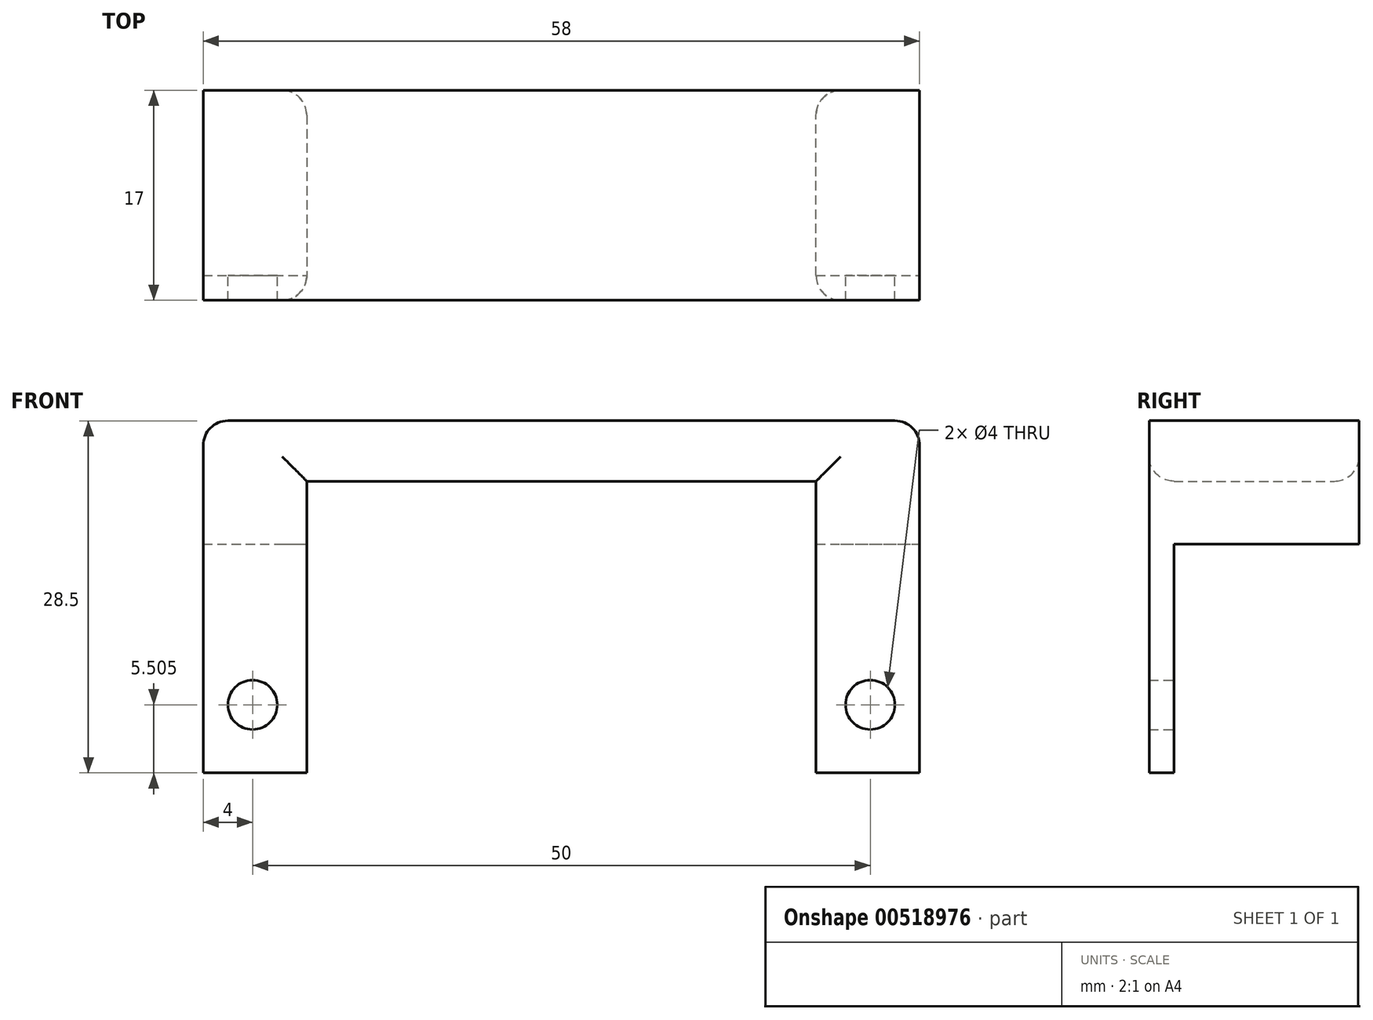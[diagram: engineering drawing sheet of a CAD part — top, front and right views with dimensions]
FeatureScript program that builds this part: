
annotation { "Feature Type Name" : "Feature", "Feature Type Description" : "" }
export const myFeature = defineFeature(function(context is Context, id is Id, definition is map)
    precondition{}
    {
        {
            var Q0;
            Q0=qCreatedBy(makeId("Front.planeOp"),FACE);
            var sketch = newSketch(context, id + "F0", { "sketchPlane" : qUnion([Q0])});
            skLineSegment(sketch, "E0.bottom", {"start": v(-17.8, 17.5) * mm, "end": v(40.2, 17.5) * mm});
            skLineSegment(sketch, "E0.left", {"start": v(-17.8, 17.5) * mm, "end": v(-17.8, -11) * mm});
            skLineSegment(sketch, "E0.right", {"start": v(40.2, 17.5) * mm, "end": v(40.2, -11) * mm});
            skLineSegment(sketch, "E1", {"start": v(-17.8, 7.5) * mm, "end": v(40.2, 7.5) * mm, "construction": true});
            skCircle(sketch, "E2", {"center": v(-13.8, -5.5) * mm, "radius": 2 * mm});
            skCircle(sketch, "E3", {"center": v(36.2, -5.5) * mm, "radius": 2 * mm});
            skLineSegment(sketch, "E4.top", {"start": v(-9.42, 12.6) * mm, "end": v(31.8, 12.6) * mm});
            skLineSegment(sketch, "E4.left", {"start": v(-9.42, -11) * mm, "end": v(-9.42, 12.6) * mm});
            skLineSegment(sketch, "E4.right", {"start": v(31.8, -11) * mm, "end": v(31.8, 12.6) * mm});
            skLineSegment(sketch, "E5", {"start": v(-9.42, -11) * mm, "end": v(-17.8, -11) * mm});
            skLineSegment(sketch, "E6", {"start": v(31.8, -11) * mm, "end": v(40.2, -11) * mm});
            skSolve(sketch);
        }
        {
            var Q0;
            Q0=makeQuery(id+"F0.imprint","IMPRINT",FACE,{"disambiguationData":[TD([[makeQuery(id+"F0.imprint","IMPRINT",EDGE,{"derivedFrom":sQuery(id+"F0.wireOp",EDGE,"E0.bottom")}),-1.0]])]});
            extrude(context, id + "F1", {"entities" : qUnion([Q0]), "depth" : 2 * mm, "offsetDistance" : 25 * mm});
        }
        {
            var Q0;
            Q0=makeQuery(id+"F0.imprint","IMPRINT",FACE,{"disambiguationData":[TD([[makeQuery(id+"F0.imprint","IMPRINT",EDGE,{"derivedFrom":sQuery(id+"F0.wireOp",EDGE,"E0.bottom")}),-1.0]])]});
            var sketch = newSketch(context, id + "F2", { "sketchPlane" : qUnion([Q0])});
            skLineSegment(sketch, "E7", {"start": v(40.2, 7.5) * mm, "end": v(40.2, 17.5) * mm});
            skLineSegment(sketch, "E8", {"start": v(40.2, 17.5) * mm, "end": v(-17.8, 17.5) * mm});
            skLineSegment(sketch, "E9", {"start": v(-17.8, 17.5) * mm, "end": v(-17.8, 7.5) * mm});
            skLineSegment(sketch, "E10", {"start": v(-17.8, 7.5) * mm, "end": v(-9.42, 7.5) * mm});
            skLineSegment(sketch, "E11", {"start": v(-9.42, 7.5) * mm, "end": v(-9.42, 12.6) * mm});
            skLineSegment(sketch, "E12", {"start": v(-9.42, 12.6) * mm, "end": v(31.8, 12.6) * mm});
            skLineSegment(sketch, "E13", {"start": v(31.8, 12.6) * mm, "end": v(31.8, 7.5) * mm});
            skLineSegment(sketch, "E14", {"start": v(31.8, 7.5) * mm, "end": v(40.2, 7.5) * mm});
            skSolve(sketch);
        }
        {
            var Q0;
            Q0=makeQuery(id+"F2.imprint","IMPRINT",FACE,{"disambiguationData":[TD([[makeQuery(id+"F2.imprint","IMPRINT",EDGE,{"derivedFrom":sQuery(id+"F2.wireOp",EDGE,"E7")}),-1.0]])]});
            extrude(context, id + "F3", {"entities" : qUnion([Q0]), "operationType" : NewBodyOperationType.ADD, "oppositeDirection" : true, "depth" : 15 * mm, "offsetDistance" : 25 * mm});
        }
        {
            var Q0;
            Q0=makeQuery(id+"F3.boolean.opBoolean","MERGE",EDGE,{"derivedFrom":[makeQuery(id+"F1.opExtrude","SWEPT_EDGE",EDGE,{"disambiguationData":[OSD([sQuery(id+"F0.wireOp",EDGE,"E0.bottom"),sQuery(id+"F0.wireOp",EDGE,"E0.left")])]}),makeQuery(id+"F3.opExtrude","SWEPT_EDGE",EDGE,{"disambiguationData":[OSD([sQuery(id+"F2.wireOp",EDGE,"E8"),sQuery(id+"F2.wireOp",EDGE,"E9")])]})]});
            var Q1;
            Q1=makeQuery(id+"F3.boolean.opBoolean","MERGE",EDGE,{"derivedFrom":[makeQuery(id+"F1.opExtrude","SWEPT_EDGE",EDGE,{"disambiguationData":[OSD([sQuery(id+"F0.wireOp",EDGE,"E0.bottom"),sQuery(id+"F0.wireOp",EDGE,"E0.right")])]}),makeQuery(id+"F3.opExtrude","SWEPT_EDGE",EDGE,{"disambiguationData":[OSD([sQuery(id+"F2.wireOp",EDGE,"E7"),sQuery(id+"F2.wireOp",EDGE,"E8")])]})]});
            var Q2;
            Q2=makeQuery(id+"F1.opExtrude","CAP_EDGE",EDGE,{"disambiguationData":[OSD([sQuery(id+"F0.wireOp",EDGE,"E4.top")])],"isStart":false});
            var Q3;
            Q3=makeQuery(id+"F1.opExtrude","CAP_EDGE",EDGE,{"disambiguationData":[OSD([sQuery(id+"F0.wireOp",EDGE,"E4.right")])],"isStart":false});
            var Q4;
            Q4=makeQuery(id+"F1.opExtrude","CAP_EDGE",EDGE,{"disambiguationData":[OSD([sQuery(id+"F0.wireOp",EDGE,"E4.left")])],"isStart":false});
            var Q5;
            Q5=makeQuery(id+"F3.opExtrude","CAP_EDGE",EDGE,{"disambiguationData":[OSD([sQuery(id+"F2.wireOp",EDGE,"E13")])],"isStart":false});
            var Q6;
            Q6=makeQuery(id+"F3.opExtrude","CAP_EDGE",EDGE,{"disambiguationData":[OSD([sQuery(id+"F2.wireOp",EDGE,"E12")])],"isStart":false});
            var Q7;
            Q7=makeQuery(id+"F3.opExtrude","CAP_EDGE",EDGE,{"disambiguationData":[OSD([sQuery(id+"F2.wireOp",EDGE,"E11")])],"isStart":false});
            fillet(context, id + "F4", {"entities" : qUnion([Q0, Q1, Q2, Q3, Q4, Q5, Q6, Q7]), "radius" : 2 * mm, "tangentPropagation" : true, "allowEdgeOverflow" : false});
        }
    });
